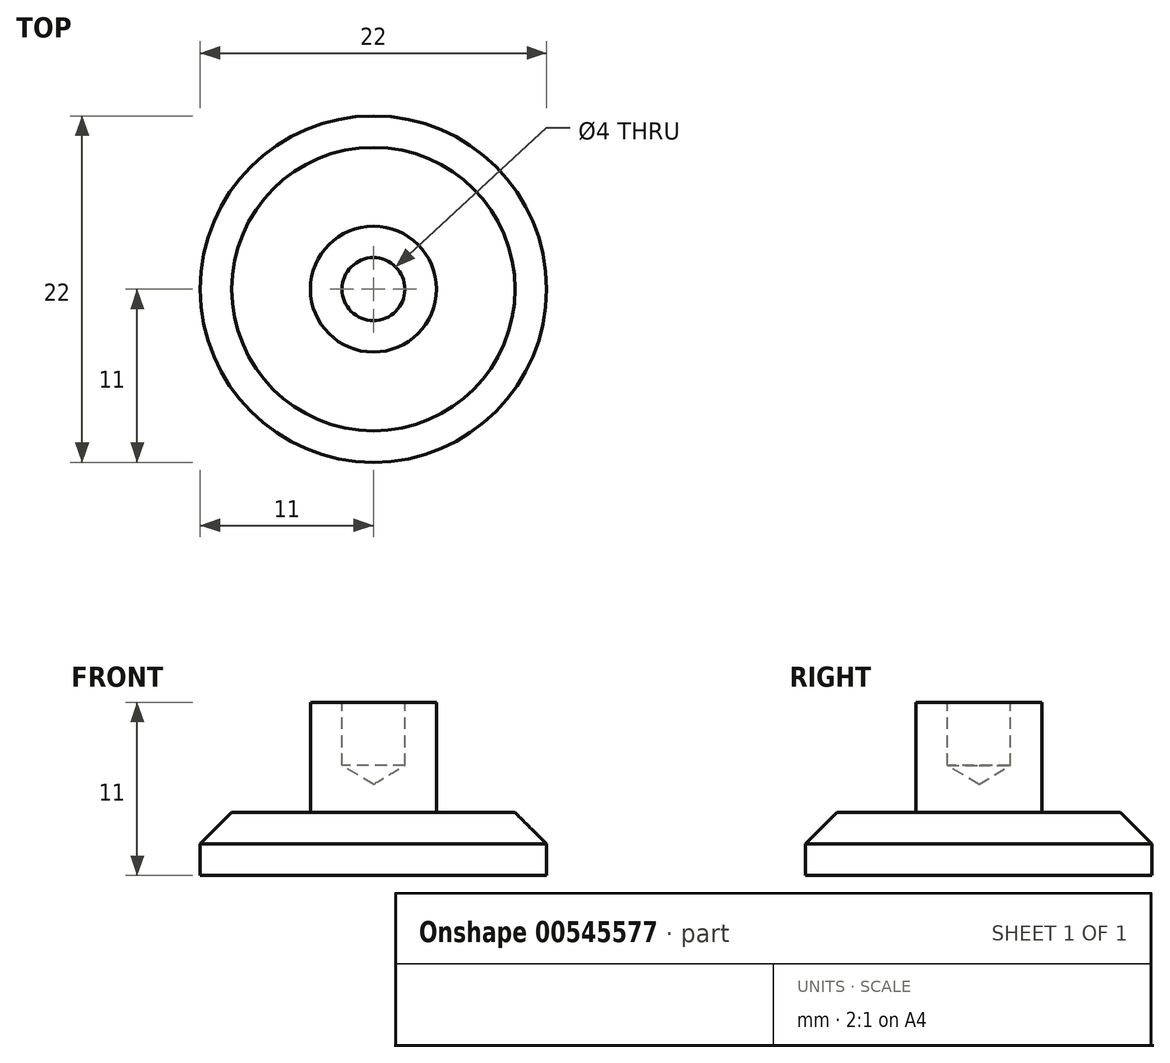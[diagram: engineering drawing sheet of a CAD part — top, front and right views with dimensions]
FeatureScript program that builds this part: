
annotation { "Feature Type Name" : "Feature", "Feature Type Description" : "" }
export const myFeature = defineFeature(function(context is Context, id is Id, definition is map)
    precondition{}
    {
        {
            var Q0;
            Q0=qCreatedBy(makeId("Top.planeOp"),FACE);
            var sketch = newSketch(context, id + "F0", { "sketchPlane" : qUnion([Q0])});
            skCircle(sketch, "E0", {"center": v(0, 0) * mm, "radius": 11 * mm});
            skSolve(sketch);
        }
        {
            var Q0;
            Q0=makeQuery(id+"F0.imprint","IMPRINT",FACE,{"disambiguationData":[TD([[makeQuery(id+"F0.imprint","IMPRINT",EDGE,{"derivedFrom":sQuery(id+"F0.wireOp",EDGE,"E0")}),1.0]])]});
            extrude(context, id + "F1", {"entities" : qUnion([Q0]), "depth" : 4 * mm, "offsetDistance" : 25 * mm});
        }
        {
            var Q0;
            Q0=makeQuery(id+"F1.opExtrude","CAP_EDGE",EDGE,{"disambiguationData":[OSD([sQuery(id+"F0.wireOp",EDGE,"E0")])],"isStart":false});
            chamfer(context, id + "F2", {"entities" : qUnion([Q0]), "width" : 2 * mm});
        }
        {
            var Q0;
            Q0=makeQuery(id+"F1.opExtrude","CAP_FACE",FACE,{"disambiguationData":[OSD([sQuery(id+"F0.wireOp",EDGE,"E0")])],"isStart":false});
            var sketch = newSketch(context, id + "F3", { "sketchPlane" : qUnion([Q0])});
            skCircle(sketch, "E1", {"center": v(0, 0) * mm, "radius": 4 * mm});
            skSolve(sketch);
        }
        {
            var Q0;
            Q0=makeQuery(id+"F3.imprint","IMPRINT",FACE,{"disambiguationData":[TD([[makeQuery(id+"F3.imprint","IMPRINT",EDGE,{"derivedFrom":sQuery(id+"F3.wireOp",EDGE,"E1")}),1.0]])]});
            extrude(context, id + "F4", {"entities" : qUnion([Q0]), "operationType" : NewBodyOperationType.ADD, "depth" : 7 * mm, "offsetDistance" : 25 * mm});
        }
        {
            var Q0;
            Q0=makeQuery(id+"F4.opExtrude","CAP_FACE",FACE,{"disambiguationData":[OSD([sQuery(id+"F3.wireOp",EDGE,"E1")])],"isStart":false});
            var sketch = newSketch(context, id + "F5", { "sketchPlane" : qUnion([Q0])});
            skPoint(sketch, "E2", {"position": v(0, 0) * mm});
            skSolve(sketch);
        }
        {
            var Q0;
            Q0=sQuery(id+"F5.wireOp",VERTEX,"E2");
            var Q1;
            Q1=makeQuery(id+"F1.opExtrude","SWEPT_BODY",BODY,{"disambiguationData":[OSD([sQuery(id+"F0.wireOp",EDGE,"E0")])]});
            hole(context, id + "F6", {"style" : HoleStyle.SIMPLE, "endStyle" : HoleEndStyle.BLIND, "holeDiameter" : 4 * mm, "holeDepth" : 4 * mm, "isTappedThrough" : true, "tappedDepth" : 12 * mm, "tapClearance" : 3, "locations" : qUnion([Q0]), "scope" : qUnion([Q1])});
        }
    });
